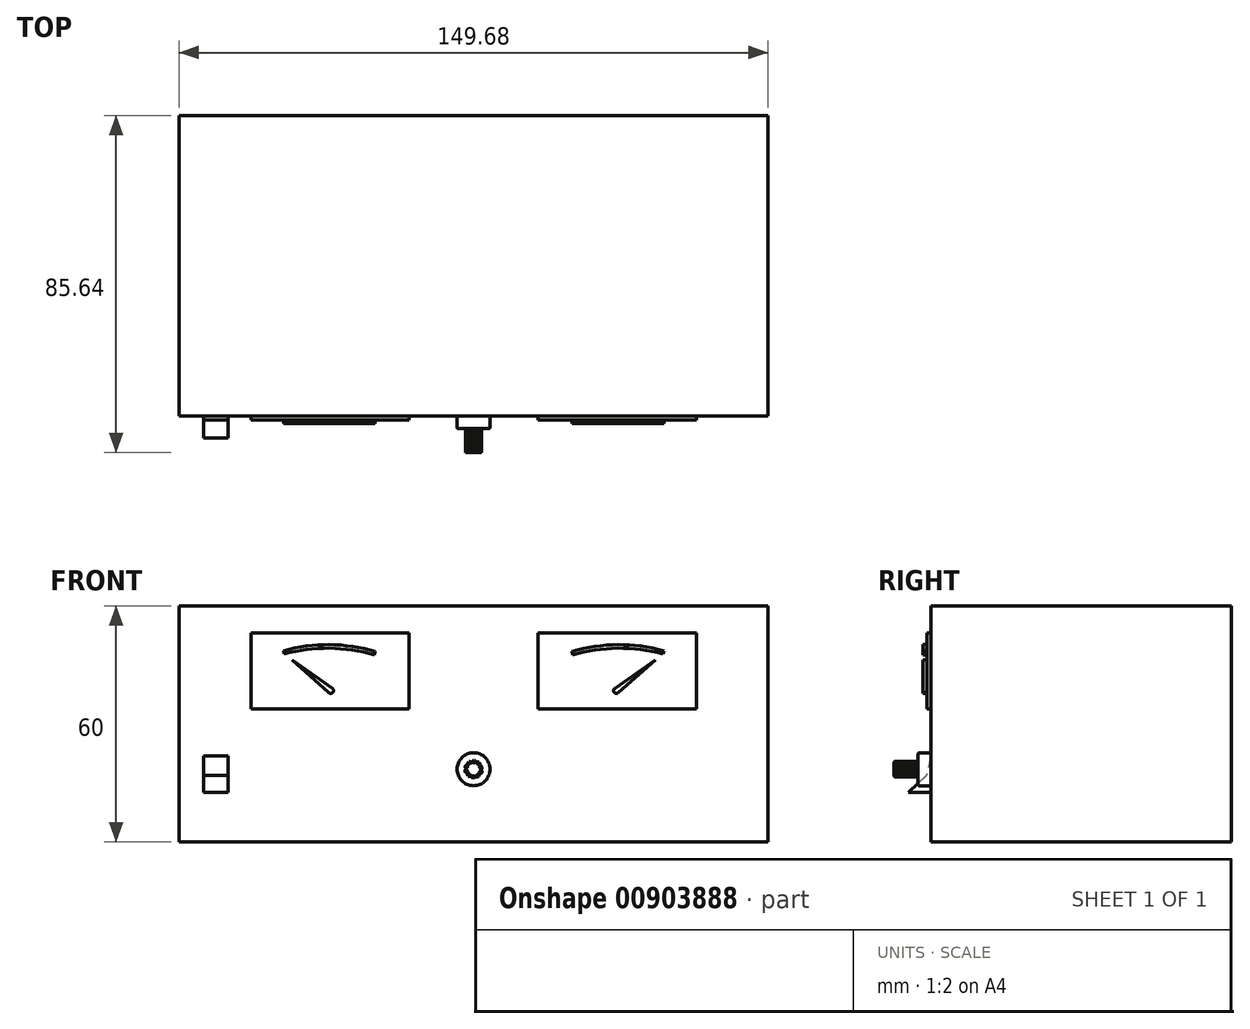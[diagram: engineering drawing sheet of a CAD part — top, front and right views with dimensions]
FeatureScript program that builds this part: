
annotation { "Feature Type Name" : "Feature", "Feature Type Description" : "" }
export const myFeature = defineFeature(function(context is Context, id is Id, definition is map)
    precondition{}
    {
        {
            var Q0;
            Q0=qCreatedBy(makeId("Top.planeOp"),FACE);
            var sketch = newSketch(context, id + "F0", { "sketchPlane" : qUnion([Q0])});
            skLineSegment(sketch, "E0.bottom", {"start": v(-74.84, 38.17) * mm, "end": v(74.84, 38.17) * mm});
            skLineSegment(sketch, "E0.top", {"start": v(-74.84, -38.17) * mm, "end": v(74.84, -38.17) * mm});
            skLineSegment(sketch, "E0.left", {"start": v(-74.84, 38.17) * mm, "end": v(-74.84, -38.17) * mm});
            skLineSegment(sketch, "E0.right", {"start": v(74.84, 38.17) * mm, "end": v(74.84, -38.17) * mm});
            skPoint(sketch, "E0.middle", {"position": v(0, 0) * mm});
            skSolve(sketch);
        }
        {
            var Q0;
            Q0 = qSketchRegion(id + "F0", true);
            extrude(context, id + "F1", {"entities" : qUnion([Q0]), "depth" : 60 * mm, "offsetDistance" : 25 * mm});
        }
        {
            var Q0;
            Q0=makeQuery(id+"F1.opExtrude","SWEPT_FACE",FACE,{"disambiguationData":[OSD([sQuery(id+"F0.wireOp",EDGE,"E0.top")])]});
            var sketch = newSketch(context, id + "F2", { "sketchPlane" : qUnion([Q0])});
            skLineSegment(sketch, "E1.bottom", {"start": v(-56.57, 53.1) * mm, "end": v(-16.37, 53.1) * mm});
            skLineSegment(sketch, "E1.top", {"start": v(-56.57, 33.83) * mm, "end": v(-16.37, 33.83) * mm});
            skLineSegment(sketch, "E1.left", {"start": v(-56.57, 53.1) * mm, "end": v(-56.57, 33.83) * mm});
            skLineSegment(sketch, "E1.right", {"start": v(-16.37, 53.1) * mm, "end": v(-16.37, 33.83) * mm});
            skLineSegment(sketch, "E2.MirrorCS", {"start": v(56.57, 53.1) * mm, "end": v(16.37, 53.1) * mm});
            skLineSegment(sketch, "E3.MirrorCS", {"start": v(16.37, 53.1) * mm, "end": v(16.37, 33.83) * mm});
            skLineSegment(sketch, "E4.MirrorCS", {"start": v(56.57, 53.1) * mm, "end": v(56.57, 33.83) * mm});
            skLineSegment(sketch, "E5.MirrorCS", {"start": v(56.57, 33.83) * mm, "end": v(16.37, 33.83) * mm});
            skSolve(sketch);
        }
        {
            var Q0;
            Q0 = qSketchRegion(id + "F2", true);
            extrude(context, id + "F3", {"entities" : qUnion([Q0]), "depth" : 1 * mm, "offsetDistance" : 25 * mm});
        }
        {
            var Q0;
            Q0=makeQuery(id+"F1.opExtrude","SWEPT_FACE",FACE,{"disambiguationData":[OSD([sQuery(id+"F0.wireOp",EDGE,"E0.top")])]});
            var sketch = newSketch(context, id + "F4", { "sketchPlane" : qUnion([Q0])});
            skCircle(sketch, "E6", {"center": v(0, 18.52) * mm, "radius": 4.19 * mm});
            skSolve(sketch);
        }
        {
            var Q0;
            Q0 = qSketchRegion(id + "F4", true);
            extrude(context, id + "F5", {"entities" : qUnion([Q0]), "operationType" : NewBodyOperationType.ADD, "depth" : 3.2 * mm, "offsetDistance" : 25 * mm});
        }
        {
            var Q0;
            Q0=makeQuery(id+"F5.opExtrude","CAP_FACE",FACE,{"disambiguationData":[OSD([sQuery(id+"F4.wireOp",EDGE,"E6")])],"isStart":false});
            var sketch = newSketch(context, id + "F6", { "sketchPlane" : qUnion([Q0])});
            skArc(sketch, "E7", {"start": v(-0.34, 20.47) * mm, "mid": v(-0.1, 16.54) * mm, "end": v(0.54, 20.42) * mm});
            skArc(sketch, "E8", {"start": v(-0.34, 20.47) * mm, "mid": v(0.09, 20.15) * mm, "end": v(0.54, 20.42) * mm});
            skSolve(sketch);
        }
        {
            var Q0;
            Q0 = qSketchRegion(id + "F6", true);
            extrude(context, id + "F7", {"entities" : qUnion([Q0]), "operationType" : NewBodyOperationType.ADD, "depth" : 6.1 * mm, "offsetDistance" : 25 * mm});
        }
        {
            var Q0;
            Q0=makeQuery(id+"F7.opExtrude","SWEPT_FACE",FACE,{"disambiguationData":[OSD([sQuery(id+"F6.wireOp",EDGE,"E8")])]});
            var Q1;
            Q1=makeQuery(id+"F7.opExtrude","SWEPT_FACE",FACE,{"disambiguationData":[OSD([sQuery(id+"F6.wireOp",EDGE,"E7")])]});
            circularPattern(context, id + "F8", {"patternType" : PatternType.FACE, "faces" : qUnion([Q0]), "axis" : qUnion([Q1]), "angle" : 360 * degree, "instanceCount" : 10, "equalSpace" : true});
        }
        {
            var Q0;
            Q0=makeQuery(id+"F5.opExtrude","CAP_FACE",FACE,{"disambiguationData":[OSD([sQuery(id+"F4.wireOp",EDGE,"E6")])],"isStart":false});
            var Q1;
            Q1=makeQuery(id+"F7.opExtrude","CAP_FACE",FACE,{"disambiguationData":[OSD([sQuery(id+"F6.wireOp",EDGE,"E7"),sQuery(id+"F6.wireOp",EDGE,"E8")])],"isStart":false});
            var Q2;
            Q2=makeQuery(id+"F5.opExtrude","CAP_EDGE",EDGE,{"disambiguationData":[OSD([sQuery(id+"F4.wireOp",EDGE,"E6")])],"isStart":true});
            fillet(context, id + "F9", {"entities" : qUnion([Q0, Q1, Q2]), "radius" : 0.3 * mm, "tangentPropagation" : true, "allowEdgeOverflow" : false});
        }
        {
            var Q0;
            Q0=makeQuery(id+"F3.opExtrude","CAP_FACE",FACE,{"disambiguationData":[OSD([sQuery(id+"F2.wireOp",EDGE,"E1.bottom"),sQuery(id+"F2.wireOp",EDGE,"E1.top"),sQuery(id+"F2.wireOp",EDGE,"E1.left"),sQuery(id+"F2.wireOp",EDGE,"E1.right")])],"isStart":false});
            var sketch = newSketch(context, id + "F10", { "sketchPlane" : qUnion([Q0])});
            skArc(sketch, "E9", {"start": v(-36.81, 38.03) * mm, "mid": v(-35.76, 38.02) * mm, "end": v(-35.88, 39.06) * mm});
            skLineSegment(sketch, "E10", {"start": v(-36.81, 38.03) * mm, "end": v(-46.16, 46.31) * mm});
            skLineSegment(sketch, "E11", {"start": v(-46.16, 46.31) * mm, "end": v(-35.88, 39.06) * mm});
            skArc(sketch, "E12", {"start": v(-25.19, 47.53) * mm, "mid": v(-36.63, 49.27) * mm, "end": v(-48.12, 47.84) * mm});
            skArc(sketch, "E13", {"start": v(-25.02, 48.39) * mm, "mid": v(-36.66, 50.17) * mm, "end": v(-48.33, 48.56) * mm});
            skLineSegment(sketch, "E14", {"start": v(-48.33, 48.56) * mm, "end": v(-48.12, 47.84) * mm});
            skLineSegment(sketch, "E15", {"start": v(-25.02, 48.39) * mm, "end": v(-25.19, 47.53) * mm});
            skArc(sketch, "E16.MirrorCS", {"start": v(36.81, 38.03) * mm, "mid": v(35.76, 38.02) * mm, "end": v(35.88, 39.06) * mm});
            skLineSegment(sketch, "E17.MirrorCS", {"start": v(36.81, 38.03) * mm, "end": v(46.16, 46.31) * mm});
            skLineSegment(sketch, "E18.MirrorCS", {"start": v(46.16, 46.31) * mm, "end": v(35.88, 39.06) * mm});
            skArc(sketch, "E19.MirrorCS", {"start": v(25.02, 48.39) * mm, "mid": v(36.66, 50.17) * mm, "end": v(48.33, 48.56) * mm});
            skArc(sketch, "E20.MirrorCS", {"start": v(25.19, 47.53) * mm, "mid": v(36.63, 49.27) * mm, "end": v(48.12, 47.84) * mm});
            skLineSegment(sketch, "E21.MirrorCS", {"start": v(48.33, 48.56) * mm, "end": v(48.12, 47.84) * mm});
            skLineSegment(sketch, "E22.MirrorCS", {"start": v(25.02, 48.39) * mm, "end": v(25.19, 47.53) * mm});
            skSolve(sketch);
        }
        {
            var Q0;
            Q0 = qSketchRegion(id + "F10", true);
            extrude(context, id + "F11", {"entities" : qUnion([Q0]), "depth" : 1 * mm, "offsetDistance" : 25 * mm});
        }
        {
            var Q0;
            Q0=makeQuery(id+"F1.opExtrude","SWEPT_FACE",FACE,{"disambiguationData":[OSD([sQuery(id+"F0.wireOp",EDGE,"E0.top")])]});
            var sketch = newSketch(context, id + "F12", { "sketchPlane" : qUnion([Q0])});
            skLineSegment(sketch, "E23.bottom", {"start": v(-68.59, 21.86) * mm, "end": v(-62.38, 21.86) * mm});
            skLineSegment(sketch, "E23.top", {"start": v(-68.59, 12.67) * mm, "end": v(-62.38, 12.67) * mm});
            skLineSegment(sketch, "E23.left", {"start": v(-68.59, 21.86) * mm, "end": v(-68.59, 12.67) * mm});
            skLineSegment(sketch, "E23.right", {"start": v(-62.38, 21.86) * mm, "end": v(-62.38, 12.67) * mm});
            skSolve(sketch);
        }
        {
            var Q0;
            Q0 = qSketchRegion(id + "F12", true);
            extrude(context, id + "F13", {"entities" : qUnion([Q0]), "operationType" : NewBodyOperationType.ADD, "depth" : 5.6 * mm, "offsetDistance" : 25 * mm});
        }
        {
            var Q0;
            Q0=makeQuery(id+"F13.opExtrude","SWEPT_FACE",FACE,{"disambiguationData":[OSD([sQuery(id+"F12.wireOp",EDGE,"E23.left")])]});
            var sketch = newSketch(context, id + "F14", { "sketchPlane" : qUnion([Q0])});
            skLineSegment(sketch, "E24", {"start": v(38.17, 21.86) * mm, "end": v(39.21, 16.99) * mm});
            skLineSegment(sketch, "E25", {"start": v(39.21, 16.99) * mm, "end": v(43.77, 12.67) * mm});
            skLineSegment(sketch, "E26", {"start": v(43.77, 12.67) * mm, "end": v(43.77, 21.86) * mm});
            skLineSegment(sketch, "E27", {"start": v(43.77, 21.86) * mm, "end": v(38.17, 21.86) * mm});
            skSolve(sketch);
        }
        {
            var Q0;
            Q0 = qSketchRegion(id + "F14", true);
            extrude(context, id + "F15", {"entities" : qUnion([Q0]), "operationType" : NewBodyOperationType.REMOVE, "oppositeDirection" : true, "depth" : 6.2 * mm, "offsetDistance" : 25 * mm});
        }
    });
